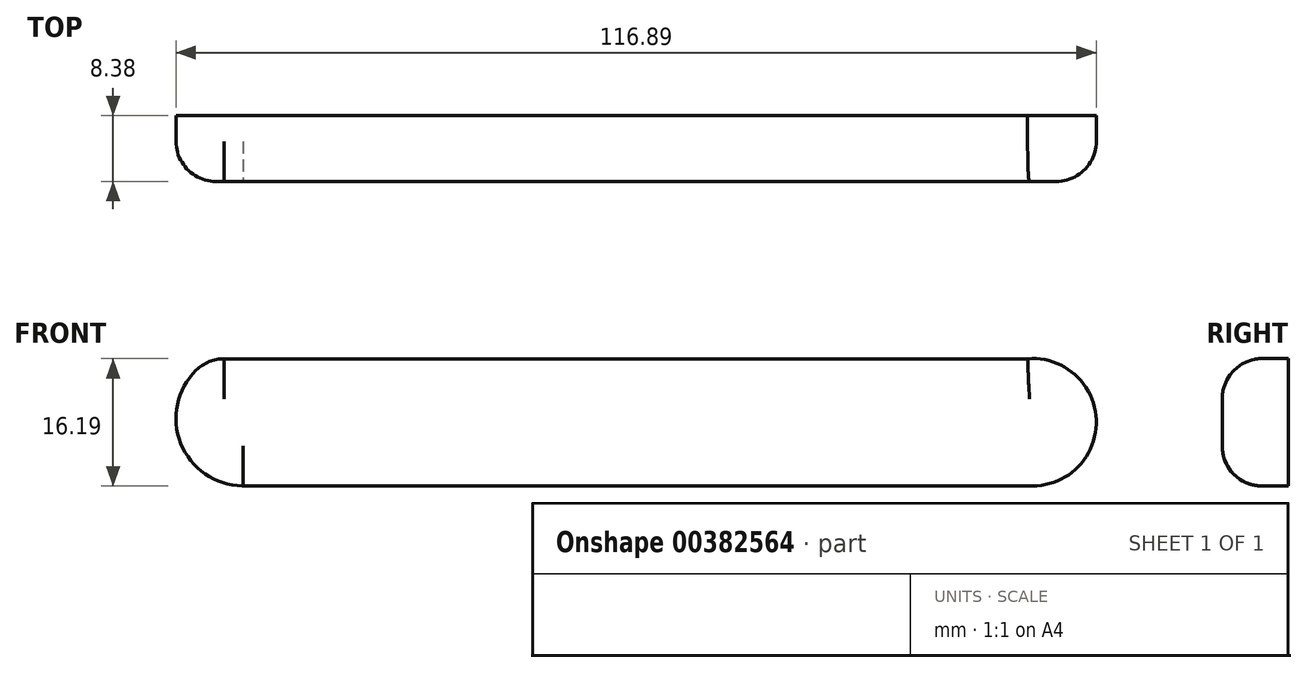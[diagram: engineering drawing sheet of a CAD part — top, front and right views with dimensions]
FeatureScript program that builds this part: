
annotation { "Feature Type Name" : "Feature", "Feature Type Description" : "" }
export const myFeature = defineFeature(function(context is Context, id is Id, definition is map)
    precondition{}
    {
        {
            var Q0;
            Q0=qCreatedBy(makeId("Front.planeOp"),FACE);
            var sketch = newSketch(context, id + "F0", { "sketchPlane" : qUnion([Q0])});
            skArc(sketch, "E0", {"start": v(-36.68, 10.82) * mm, "mid": v(-40.99, 1.22) * mm, "end": v(-32.76, -5.35) * mm});
            skLineSegment(sketch, "E1", {"start": v(-36.68, 10.82) * mm, "end": v(66.95, 10.82) * mm});
            skLineSegment(sketch, "E2", {"start": v(-32.76, -5.35) * mm, "end": v(67.57, -5.35) * mm});
            skArc(sketch, "E3", {"start": v(67.57, -5.35) * mm, "mid": v(75.66, 3.06) * mm, "end": v(66.95, 10.82) * mm});
            skSolve(sketch);
        }
        {
            var Q0;
            Q0=qSketchRegion(id+"F0",true);
            extrude(context, id + "F1", {"entities" : qUnion([Q0]), "depth" : 8.38 * mm});
        }
        {
            var Q0;
            Q0=makeQuery(id+"F1.opExtrude","CAP_EDGE",EDGE,{"disambiguationData":[OSD([sQuery(id+"F0.wireOp",EDGE,"E1")])],"isStart":false});
            var Q1;
            Q1=makeQuery(id+"F1.opExtrude","CAP_EDGE",EDGE,{"disambiguationData":[OSD([sQuery(id+"F0.wireOp",EDGE,"E2")])],"isStart":false});
            fillet(context, id + "F2", {"entities" : qUnion([Q0, Q1]), "radius" : 5.08 * mm, "tangentPropagation" : true, "allowEdgeOverflow" : false});
        }
        {
            var Q0;
            Q0=makeQuery(id+"F1.opExtrude","CAP_EDGE",EDGE,{"disambiguationData":[OSD([sQuery(id+"F0.wireOp",EDGE,"E0")])],"isStart":false});
            fillet(context, id + "F3", {"entities" : qUnion([Q0]), "radius" : 5.08 * mm, "tangentPropagation" : true, "allowEdgeOverflow" : false});
        }
    });
